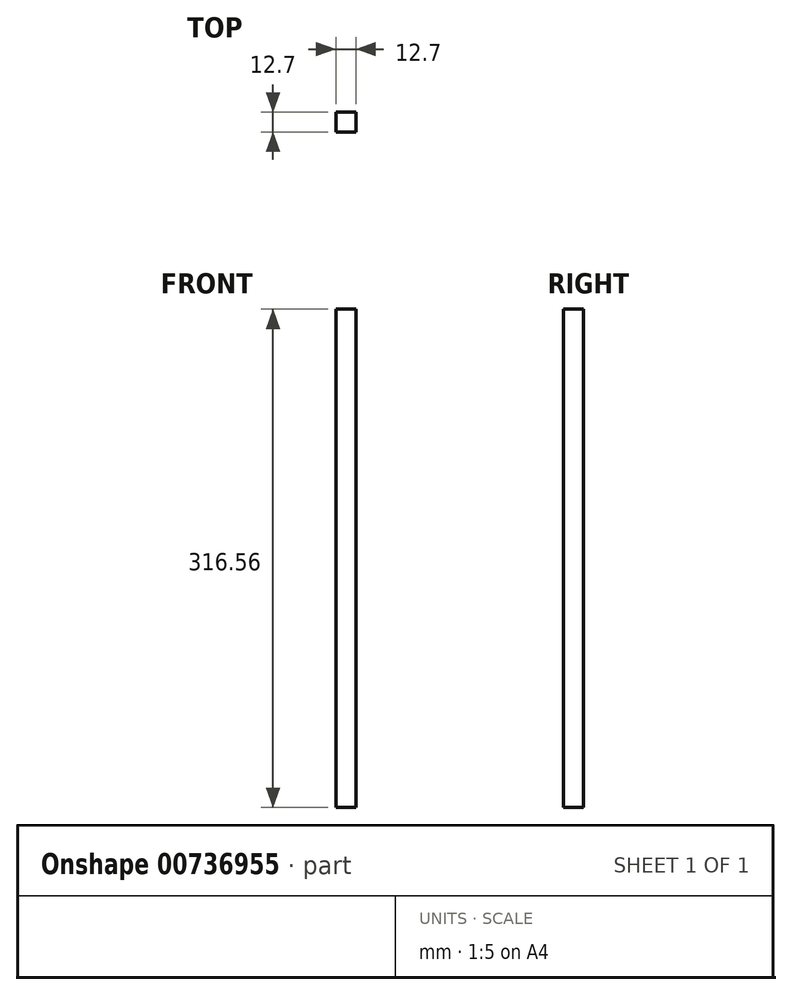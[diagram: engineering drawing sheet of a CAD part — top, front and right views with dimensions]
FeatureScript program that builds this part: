
annotation { "Feature Type Name" : "Feature", "Feature Type Description" : "" }
export const myFeature = defineFeature(function(context is Context, id is Id, definition is map)
    precondition{}
    {
        {
            var Q0;
            Q0=qCreatedBy(makeId("Front.planeOp"),FACE);
            var sketch = newSketch(context, id + "F0", { "sketchPlane" : qUnion([Q0])});
            skLineSegment(sketch, "E0.bottom", {"start": v(-6.35, 158.28) * mm, "end": v(6.35, 158.28) * mm});
            skLineSegment(sketch, "E0.top", {"start": v(-6.35, -158.28) * mm, "end": v(6.35, -158.28) * mm});
            skLineSegment(sketch, "E0.left", {"start": v(-6.35, 158.28) * mm, "end": v(-6.35, -158.28) * mm});
            skLineSegment(sketch, "E0.right", {"start": v(6.35, 158.28) * mm, "end": v(6.35, -158.28) * mm});
            skPoint(sketch, "E0.middle", {"position": v(0, 0) * mm});
            skSolve(sketch);
        }
        {
            var Q0;
            Q0=qSketchRegion(id+"F0",true);
            extrude(context, id + "F1", {"entities" : qUnion([Q0]), "depth" : 12.7 * mm, "offsetDistance" : 25.4 * mm});
        }
    });
